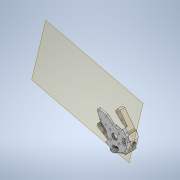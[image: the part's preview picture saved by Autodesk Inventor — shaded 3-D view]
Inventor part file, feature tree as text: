
AUTODESK INVENTOR PART (.ipt)
format: ipt  version: 2020 (Build 240168000, 168)  size: 1,202,688 bytes
history: native  units: mm
features: sketch x23, extrude x23, projected_geometry x21, plane x9, fillet x9, other x9, reference x8, thicken_offset x5, chamfer x2, mirror x1
ambient origin geometry x8: Origin, YZ Plane, XZ Plane, XY Plane, X Axis, Y Axis, Z Axis, Center Point
bodies: Solid1 (feature_tree)
feature tree (110):
  plane  "Work Plane1"
  sketch  "Sketch1"  dims[d0=70.0mm d1=58.0mm]
  plane  "Work Plane2"
  extrude  "Extrusion1"  Depth=58.0mm
  sketch  "Sketch2"  dims[d2=10.0mm d3=0.0mm d4=40.0mm]
  plane  "Work Plane3"
  extrude  "Extrusion2"  Depth=10.0mm
  sketch  "Sketch3"  dims[d5=40.0mm d6=10.0mm d7=0.0mm]
  plane  "Work Plane4"
  extrude  "Extrusion3"  Depth=10.0mm TaperAngle=0.0deg
  extrude  "Extrusion4"  Depth=10.0mm TaperAngle=0.0deg
  plane  "Work Plane5"
  extrude  "Extrusion5"  Depth=5.0mm TaperAngle=0.0deg
  extrude  "Extrusion7"  Depth=40.0mm
  extrude  "Extrusion8"  Depth=5.0mm
  extrude  "Extrusion9"  Depth=5.0mm TaperAngle=360.0deg
  extrude  "Extrusion10"  Depth=10.0mm
  fillet  "Fillet1"  Radius=4.1mm
  extrude  "Extrusion11"  Depth=5.0mm TaperAngle=0.0deg
  extrude  "Extrusion12"  Depth=5.0mm TaperAngle=0.0deg
  fillet  "Fillet3"  Radius=58.0mm
  chamfer  "Chamfer2"  Distance=5.0mm
  fillet  "Fillet4"  Radius=1.0mm
  fillet  "Fillet5"  Radius=1.2mm
  plane  "Work Plane6"
  extrude  "Extrusion16"  Depth=1.0mm
  plane  "Work Plane7"
  extrude  "Extrusion17"  Depth=10.0mm TaperAngle=0.0deg
  extrude  "Extrusion19"  Depth=10.0mm
  fillet  "Fillet6"  Radius=12.0mm
  plane  "Work Plane8"
  mirror  "Mirror1"
  extrude  "Extrusion21"  Depth=4.18879mm
  extrude  "Extrusion22"  Depth=2.0mm
  plane  "Work Plane9"
  extrude  "Extrusion23"  Depth=15.0mm TaperAngle=0.0deg
  extrude  "Extrusion24"  Depth=10.0mm
  fillet  "Fillet7"  Radius=9.0mm
  fillet  "Fillet8"  Radius=10.0mm
  thicken_offset  "Thicken1"
  thicken_offset  "Thicken2"
  chamfer  "Chamfer3"  Distance=10.0mm
  thicken_offset  "Thicken3"
  thicken_offset  "Thicken5"
  extrude  "Extrusion25"  Depth=2.0mm
  extrude  "Extrusion26"  Depth=5.0mm
  thicken_offset  "Thicken6"
  extrude  "Extrusion27"  Depth=5.0mm
  fillet  "Fillet9"  Radius=5.0mm
  fillet  "Fillet10"  Radius=1.0mm
  extrude  "Extrusion28"  Depth=1.0mm
  extrude  "Extrusion29"  Depth=1.0mm
  reference  "Reference1"
  reference  "Reference2"
  reference  "Reference3"
  projected_geometry  "Projected Loop1"
  projected_geometry  "Projected Loop2"
  sketch  "Sketch4"  dims[d8=10.0mm d9=0.0mm d10=10.0mm d11=0.0mm]
  reference  "Reference4"
  projected_geometry  "Projected Loop3"
  sketch  "Sketch5"  dims[d12=5.0mm d13=0.0mm d24=14.0mm d25=0.0mm]
  projected_geometry  "Projected Loop4"
  sketch  "Sketch8"  dims[d26=16.15mm d27=40.0mm]
  reference  "Reference5"
  sketch  "Sketch9"  dims[d28=5.0mm d29=0.0mm d30=15.0mm]
  projected_geometry  "Projected Loop7"
  sketch  "Sketch10"  dims[d31=5.0mm d32=60.0mm d34=360.0deg]
  projected_geometry  "Projected Loop8"
  sketch  "Sketch11"  dims[d36=10.0mm d37=0.0mm d38=4.0mm d39=4.1mm]
  projected_geometry  "Projected Loop9"
  sketch  "Sketch12"  dims[d40=60.0mm d42=360.0deg d44=5.0mm d45=0.0mm]
  projected_geometry  "Projected Loop10"
  projected_geometry  "Projected Loop11"
  sketch  "Sketch13"  dims[d46=2.0mm d51=5.0mm d52=0.0mm d53=58.0mm d54=5.0mm d55=0.0mm d56=1.0mm]
  projected_geometry  "Projected Loop12"
  projected_geometry  "Projected Loop13"
  sketch  "Sketch17"  dims[d57=3.0mm d58=2.0mm d59=45.0deg d69=1.2mm]
  projected_geometry  "Projected Loop15"
  sketch  "Sketch18"  dims[d70=6.0mm d71=1.0mm]
  projected_geometry  "Projected Loop16"
  sketch  "Sketch20"  dims[d72=10.0mm d73=12.0mm d74=0.0mm]
  projected_geometry  "Projected Loop18"
  sketch  "Sketch22"  dims[d75=1.0mm d76=10.0mm d77=12.0mm d78=0.0mm]
  projected_geometry  "Projected Loop19"
  sketch  "Sketch23"  dims[d87=40.0mm d88=4.18879mm]
  reference  "Reference6"
  projected_geometry  "Projected Loop20"
  projected_geometry  "Projected Loop21"
  sketch  "Sketch24"  dims[d89=10.0mm d90=0.0mm d91=2.0mm]
  reference  "Reference7"
  sketch  "Sketch25"  dims[d96=50.0mm d97=0.0mm d98=15.0mm d99=0.0mm]
  projected_geometry  "Projected Loop22"
  sketch  "Sketch26"  dims[d100=9.0mm d101=9.0mm d102=9.0mm d103=10.0mm d104=0.0mm]
  sketch  "Sketch27"  dims[d105=3.0mm d106=10.0mm d107=0.0mm]
  reference  "Reference8"
  sketch  "Sketch28"  dims[d108=10.0mm d109=2.0mm]
  projected_geometry  "Projected Loop23"
  sketch  "Sketch29"  dims[d110=5.0mm d111=5.0mm]
  projected_geometry  "Projected Loop24"
  sketch  "Sketch30"  dims[d112=5.0mm d113=5.0mm d114=5.0mm d115=2.0mm d116=45.0deg d117=1.0mm d118=1.0mm d121=1.0mm d122=1.0mm d123=10.0mm d124=0.0mm d125=0.6mm d126=16.0mm d127=10.0mm d128=0.0mm d129=0.15mm d130=0.15mm d131=24.0mm d132=0.872665mm d133=24.0mm d134=0.872665mm d135=10.0mm d136=0.0mm d137=3.0mm d138=2.0mm d139=15.0mm d140=4.0mm d141=40.0mm d143=360.0deg d145=10.0mm d146=0.0mm d147=1.0mm d148=1.0mm d149=0.0mm d33=0.872665mm d35=0.872665mm d94=0.5mm d95=0.872665mm d150=0.5mm d151=0.872665mm]
  projected_geometry  "Projected Loop25"
  parser-record x2  (decoder bookkeeping rows leaked as tree rows — omitted from the tree; the rows remain in map.json)
  other  "reducer_3.iam"
  other  "motor_h_4:1"
  other  "xl_30_1:1"
  other  "motor_r_1:1"
  other  "reducer_leg.iam"
  other  "xl_wheel_ass:2"
  other  "xl_60_ori:1"
note: 2 file-system paths scrubbed to <path> (originals preserved in map.json)
